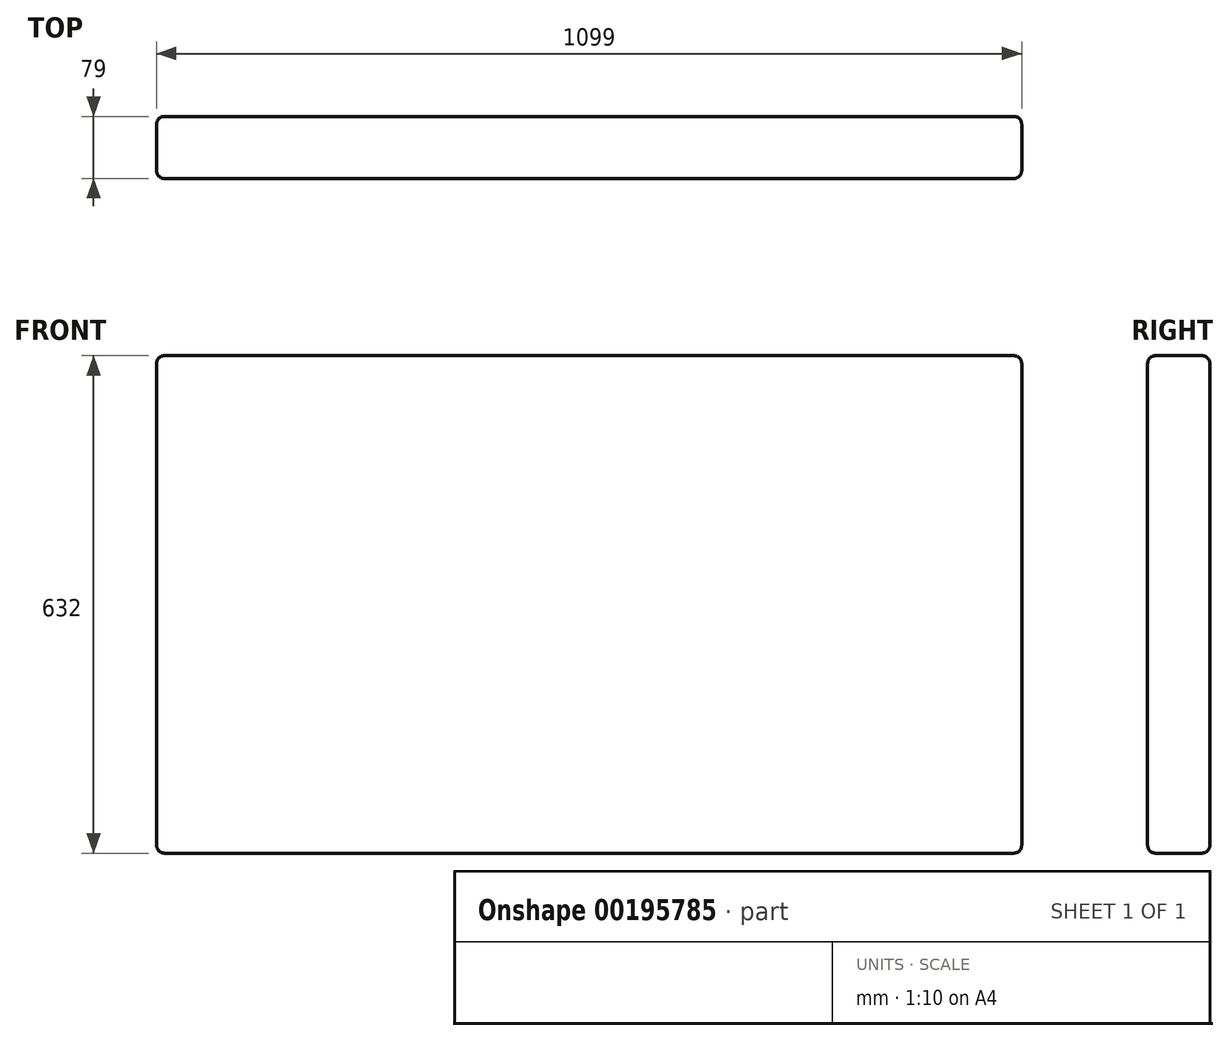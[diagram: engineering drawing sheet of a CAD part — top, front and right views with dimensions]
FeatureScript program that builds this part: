
annotation { "Feature Type Name" : "Feature", "Feature Type Description" : "" }
export const myFeature = defineFeature(function(context is Context, id is Id, definition is map)
    precondition{}
    {
        {
            var Q0;
            Q0=qCreatedBy(makeId("Top.planeOp"),FACE);
            var sketch = newSketch(context, id + "F0", { "sketchPlane" : qUnion([Q0])});
            skLineSegment(sketch, "E0.bottom", {"start": v(-196.05, 45.8) * mm, "end": v(902.95, 45.8) * mm});
            skLineSegment(sketch, "E0.top", {"start": v(-196.05, -33.2) * mm, "end": v(902.95, -33.2) * mm});
            skLineSegment(sketch, "E0.left", {"start": v(-196.05, 45.8) * mm, "end": v(-196.05, -33.2) * mm});
            skLineSegment(sketch, "E0.right", {"start": v(902.95, 45.8) * mm, "end": v(902.95, -33.2) * mm});
            skSolve(sketch);
        }
        {
            var Q0;
            Q0=makeQuery(id+"F0.imprint","IMPRINT",FACE,{"disambiguationData":[TD([[makeQuery(id+"F0.imprint","IMPRINT",EDGE,{"derivedFrom":sQuery(id+"F0.wireOp",EDGE,"E0.bottom")}),-1.0]])]});
            extrude(context, id + "F1", {"entities" : qUnion([Q0]), "depth" : 632 * mm});
        }
        {
            var Q0;
            Q0=makeQuery(id+"F1.opExtrude","CAP_FACE",FACE,{"disambiguationData":[OSD([sQuery(id+"F0.wireOp",EDGE,"E0.bottom"),sQuery(id+"F0.wireOp",EDGE,"E0.top"),sQuery(id+"F0.wireOp",EDGE,"E0.left"),sQuery(id+"F0.wireOp",EDGE,"E0.right")])],"isStart":false});
            var Q1;
            Q1=makeQuery(id+"F1.opExtrude","CAP_EDGE",EDGE,{"disambiguationData":[OSD([sQuery(id+"F0.wireOp",EDGE,"E0.bottom")])],"isStart":false});
            var Q2;
            Q2=makeQuery(id+"F1.opExtrude","CAP_EDGE",EDGE,{"disambiguationData":[OSD([sQuery(id+"F0.wireOp",EDGE,"E0.left")])],"isStart":false});
            var Q3;
            Q3=makeQuery(id+"F1.opExtrude","CAP_EDGE",EDGE,{"disambiguationData":[OSD([sQuery(id+"F0.wireOp",EDGE,"E0.right")])],"isStart":false});
            var Q4;
            Q4=makeQuery(id+"F1.opExtrude","SWEPT_EDGE",EDGE,{"disambiguationData":[OSD([sQuery(id+"F0.wireOp",EDGE,"E0.top"),sQuery(id+"F0.wireOp",EDGE,"E0.left")])]});
            var Q5;
            Q5=makeQuery(id+"F1.opExtrude","CAP_EDGE",EDGE,{"disambiguationData":[OSD([sQuery(id+"F0.wireOp",EDGE,"E0.top")])],"isStart":true});
            var Q6;
            Q6=makeQuery(id+"F1.opExtrude","SWEPT_EDGE",EDGE,{"disambiguationData":[OSD([sQuery(id+"F0.wireOp",EDGE,"E0.top"),sQuery(id+"F0.wireOp",EDGE,"E0.right")])]});
            var Q7;
            Q7=makeQuery(id+"F1.opExtrude","SWEPT_EDGE",EDGE,{"disambiguationData":[OSD([sQuery(id+"F0.wireOp",EDGE,"E0.bottom"),sQuery(id+"F0.wireOp",EDGE,"E0.right")])]});
            var Q8;
            Q8=makeQuery(id+"F1.opExtrude","CAP_EDGE",EDGE,{"disambiguationData":[OSD([sQuery(id+"F0.wireOp",EDGE,"E0.top")])],"isStart":false});
            var Q9;
            Q9=makeQuery(id+"F1.opExtrude","CAP_EDGE",EDGE,{"disambiguationData":[OSD([sQuery(id+"F0.wireOp",EDGE,"E0.right")])],"isStart":true});
            var Q10;
            Q10=makeQuery(id+"F1.opExtrude","CAP_FACE",FACE,{"disambiguationData":[OSD([sQuery(id+"F0.wireOp",EDGE,"E0.bottom"),sQuery(id+"F0.wireOp",EDGE,"E0.top"),sQuery(id+"F0.wireOp",EDGE,"E0.left"),sQuery(id+"F0.wireOp",EDGE,"E0.right")])],"isStart":true});
            var Q11;
            Q11=makeQuery(id+"F1.opExtrude","SWEPT_EDGE",EDGE,{"disambiguationData":[OSD([sQuery(id+"F0.wireOp",EDGE,"E0.bottom"),sQuery(id+"F0.wireOp",EDGE,"E0.left")])]});
            fillet(context, id + "F2", {"entities" : qUnion([Q0, Q1, Q2, Q3, Q4, Q5, Q6, Q7, Q8, Q9, Q10, Q11]), "radius" : 10 * mm, "tangentPropagation" : true, "allowEdgeOverflow" : false});
        }
    });
